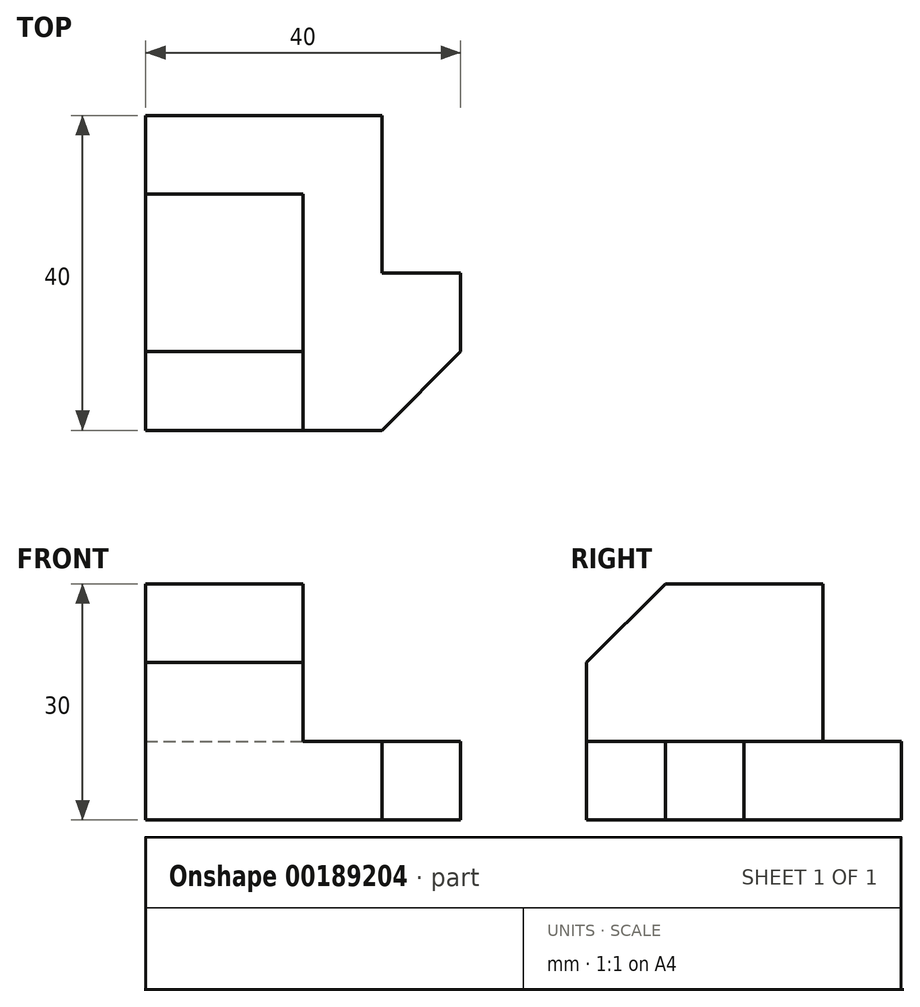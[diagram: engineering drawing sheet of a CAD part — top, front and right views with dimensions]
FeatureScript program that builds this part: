
annotation { "Feature Type Name" : "Feature", "Feature Type Description" : "" }
export const myFeature = defineFeature(function(context is Context, id is Id, definition is map)
    precondition{}
    {
        {
            var Q0;
            Q0=qCreatedBy(makeId("Top.planeOp"),FACE);
            var sketch = newSketch(context, id + "F0", { "sketchPlane" : qUnion([Q0])});
            skLineSegment(sketch, "E0", {"start": v(0, 0) * mm, "end": v(0, 40) * mm});
            skLineSegment(sketch, "E1", {"start": v(0, 40) * mm, "end": v(30, 40) * mm});
            skLineSegment(sketch, "E2", {"start": v(30, 40) * mm, "end": v(30, 20) * mm});
            skLineSegment(sketch, "E3", {"start": v(30, 20) * mm, "end": v(40, 20) * mm});
            skLineSegment(sketch, "E4", {"start": v(40, 20) * mm, "end": v(40, 10) * mm});
            skLineSegment(sketch, "E5", {"start": v(40, 10) * mm, "end": v(30, 0) * mm});
            skLineSegment(sketch, "E6", {"start": v(30, 0) * mm, "end": v(0, 0) * mm});
            skSolve(sketch);
        }
        {
            var Q0;
            Q0=makeQuery(id+"F0.imprint","IMPRINT",FACE,{"disambiguationData":[TD([[makeQuery(id+"F0.imprint","IMPRINT",EDGE,{"derivedFrom":sQuery(id+"F0.wireOp",EDGE,"E0")}),-1.0]])]});
            extrude(context, id + "F1", {"entities" : qUnion([Q0]), "depth" : 10 * mm});
        }
        {
            var Q0;
            Q0=makeQuery(id+"F1.opExtrude","CAP_FACE",FACE,{"disambiguationData":[OSD([sQuery(id+"F0.wireOp",EDGE,"E0"),sQuery(id+"F0.wireOp",EDGE,"E1"),sQuery(id+"F0.wireOp",EDGE,"E2"),sQuery(id+"F0.wireOp",EDGE,"E3"),sQuery(id+"F0.wireOp",EDGE,"E4"),sQuery(id+"F0.wireOp",EDGE,"E5"),sQuery(id+"F0.wireOp",EDGE,"E6")])],"isStart":false});
            var sketch = newSketch(context, id + "F2", { "sketchPlane" : qUnion([Q0])});
            skLineSegment(sketch, "E7.bottom", {"start": v(0, 0) * mm, "end": v(20, 0) * mm});
            skLineSegment(sketch, "E7.top", {"start": v(0, 30) * mm, "end": v(20, 30) * mm});
            skLineSegment(sketch, "E7.left", {"start": v(0, 0) * mm, "end": v(0, 30) * mm});
            skLineSegment(sketch, "E7.right", {"start": v(20, 0) * mm, "end": v(20, 30) * mm});
            skSolve(sketch);
        }
        {
            var Q0;
            Q0=makeQuery(id+"F2.imprint","IMPRINT",FACE,{"disambiguationData":[TD([[makeQuery(id+"F2.imprint","IMPRINT",EDGE,{"derivedFrom":sQuery(id+"F2.wireOp",EDGE,"E7.bottom")}),-1.0]])]});
            extrude(context, id + "F3", {"entities" : qUnion([Q0]), "operationType" : NewBodyOperationType.ADD, "depth" : 20 * mm});
        }
        {
            var Q0;
            Q0=makeQuery(id+"F3.opExtrude","CAP_EDGE",EDGE,{"disambiguationData":[OSD([sQuery(id+"F2.wireOp",EDGE,"E7.bottom")])],"isStart":false});
            chamfer(context, id + "F4", {"entities" : qUnion([Q0]), "width" : 10 * mm, "tangentPropagation" : true});
        }
    });
